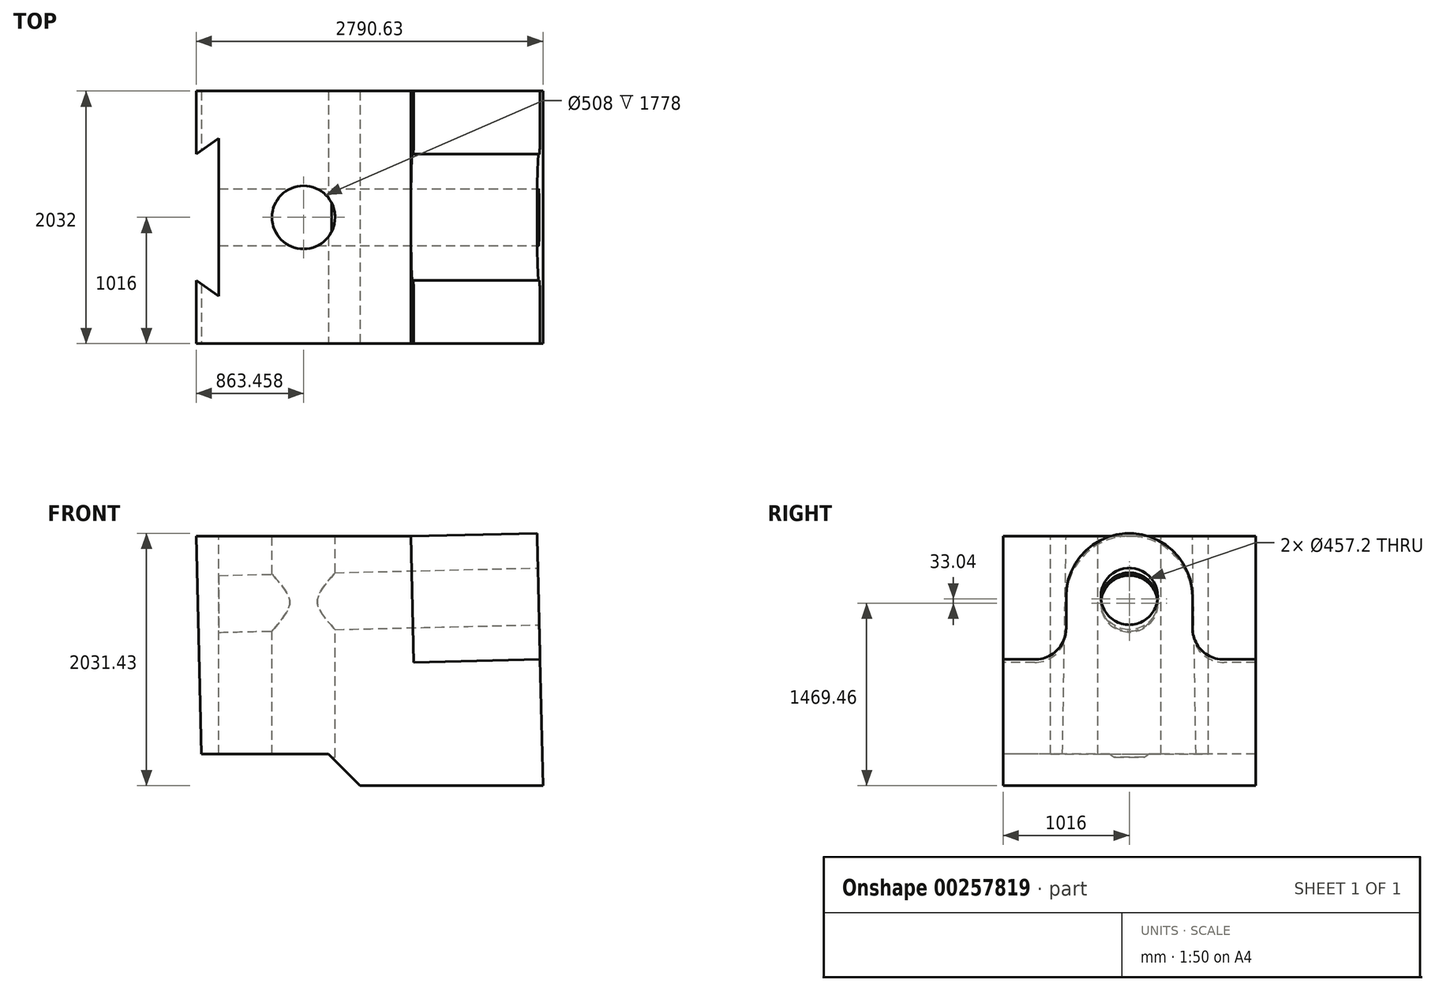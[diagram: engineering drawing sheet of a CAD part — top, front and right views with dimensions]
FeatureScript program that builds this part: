
annotation { "Feature Type Name" : "Feature", "Feature Type Description" : "" }
export const myFeature = defineFeature(function(context is Context, id is Id, definition is map)
    precondition{}
    {
        {
            var Q0;
            Q0=qCreatedBy(makeId("Front.planeOp"),FACE);
            var sketch = newSketch(context, id + "F0", { "sketchPlane" : qUnion([Q0])});
            skLineSegment(sketch, "E0", {"start": v(-1059.54, -45.61) * mm, "end": v(413.66, -45.61) * mm});
            skLineSegment(sketch, "E1", {"start": v(413.66, -45.61) * mm, "end": v(365.66, 1985.82) * mm});
            skLineSegment(sketch, "E2", {"start": v(365.66, 1985.82) * mm, "end": v(-2377.54, 1985.82) * mm});
            skLineSegment(sketch, "E3", {"start": v(-2377.54, 1985.82) * mm, "end": v(-2335.54, 208.32) * mm});
            skLineSegment(sketch, "E4", {"start": v(-1059.54, -45.61) * mm, "end": v(-1313.47, 208.32) * mm});
            skLineSegment(sketch, "E5", {"start": v(-2335.54, 208.32) * mm, "end": v(-1313.47, 208.32) * mm});
            skSolve(sketch);
        }
        {
            var Q0;
            Q0 = qSketchRegion(id + "F0", true);
            extrude(context, id + "F1", {"entities" : qUnion([Q0]), "oppositeDirection" : true, "depth" : 2032 * mm});
        }
        {
            var Q0;
            Q0=makeQuery(id+"F1.opExtrude","SWEPT_FACE",FACE,{"disambiguationData":[OSD([sQuery(id+"F0.wireOp",EDGE,"E1")])]});
            var sketch = newSketch(context, id + "F2", { "sketchPlane" : qUnion([Q0])});
            skLineSegment(sketch, "E6", {"start": v(1016, -55.37) * mm, "end": v(1016, 2378.05) * mm, "construction": true});
            skPoint(sketch, "E6.endSnap0", {"position": v(1016, 1976.63) * mm});
            skArc(sketch, "E7", {"start": v(1524, 1468.63) * mm, "mid": v(1016, 1976.63) * mm, "end": v(508, 1468.63) * mm});
            skLineSegment(sketch, "E8", {"start": v(2306.5, 960.63) * mm, "end": v(1524, 960.63) * mm});
            skLineSegment(sketch, "E9", {"start": v(1524, 1468.63) * mm, "end": v(1524, 960.63) * mm});
            skLineSegment(sketch, "E10", {"start": v(508, 1468.63) * mm, "end": v(508, 960.63) * mm});
            skLineSegment(sketch, "E11.trimOffspring", {"start": v(508, 960.63) * mm, "end": v(-735.03, 960.63) * mm});
            skLineSegment(sketch, "E12", {"start": v(0, 1976.63) * mm, "end": v(0, 960.63) * mm});
            skLineSegment(sketch, "E13", {"start": v(0, 1976.63) * mm, "end": v(2032, 1976.63) * mm});
            skLineSegment(sketch, "E14", {"start": v(2032, 1976.63) * mm, "end": v(2032, 960.63) * mm});
            skSolve(sketch);
        }
        {
            var Q0;
            Q0 = qSketchRegion(id + "F2", true);
            var Q1;
            Q1=makeQuery(id+"F1.opExtrude","SWEPT_FACE",FACE,{"disambiguationData":[OSD([sQuery(id+"F0.wireOp",EDGE,"E2")])]});
            extrude(context, id + "F3", {"entities" : qUnion([Q0, Q1]), "operationType" : NewBodyOperationType.REMOVE, "oppositeDirection" : true, "depth" : 1016 * mm});
        }
        {
            var Q0;
            Q0=makeQuery(id+"F3.boolean.opBoolean","COPY",EDGE,{"derivedFrom":makeQuery(id+"F3.opExtrude","SWEPT_EDGE",EDGE,{"disambiguationData":[OSD([sQuery(id+"F2.wireOp",EDGE,"E10"),sQuery(id+"F2.wireOp",EDGE,"E11.trimOffspring")])]})});
            fillet(context, id + "F4", {"entities" : qUnion([Q0]), "radius" : 254 * mm, "tangentPropagation" : true, "allowEdgeOverflow" : false});
        }
        {
            var Q0;
            Q0=makeQuery(id+"F3.boolean.opBoolean","COPY",EDGE,{"derivedFrom":makeQuery(id+"F3.opExtrude","SWEPT_EDGE",EDGE,{"disambiguationData":[OSD([sQuery(id+"F2.wireOp",EDGE,"E8"),sQuery(id+"F2.wireOp",EDGE,"E9")])]})});
            fillet(context, id + "F5", {"entities" : qUnion([Q0]), "radius" : 254 * mm, "tangentPropagation" : true, "allowEdgeOverflow" : false});
        }
        {
            var Q0;
            Q0=makeQuery(id+"F1.opExtrude","SWEPT_FACE",FACE,{"disambiguationData":[OSD([sQuery(id+"F0.wireOp",EDGE,"E1")])]});
            var sketch = newSketch(context, id + "F6", { "sketchPlane" : qUnion([Q0])});
            skCircle(sketch, "E15", {"center": v(1016, 1468.63) * mm, "radius": 228.6 * mm});
            skSolve(sketch);
        }
        {
            var Q0;
            Q0 = qSketchRegion(id + "F6", true);
            extrude(context, id + "F7", {"entities" : qUnion([Q0]), "operationType" : NewBodyOperationType.REMOVE, "oppositeDirection" : true, "depth" : 2743.2 * mm});
        }
        {
            var Q0;
            Q0=makeQuery(id+"F3.boolean.opBoolean","COPY",FACE,{"derivedFrom":makeQuery(id+"F3.opExtrude","CAP_FACE",FACE,{"disambiguationData":[OSD([sQuery(id+"F0.wireOp",EDGE,"E2")]),OD(0.0)],"isStart":false})});
            var sketch = newSketch(context, id + "F8", { "sketchPlane" : qUnion([Q0])});
            skLineSegment(sketch, "E16", {"start": v(-1513.51, 2032) * mm, "end": v(-1513.51, 551.9) * mm, "construction": true});
            skLineSegment(sketch, "E17", {"start": v(-2376.97, 1016) * mm, "end": v(-1513.51, 1016) * mm, "construction": true});
            skCircle(sketch, "E18", {"center": v(-1513.51, 1016) * mm, "radius": 254 * mm});
            skSolve(sketch);
        }
        {
            var Q0;
            Q0 = qSketchRegion(id + "F8", true);
            extrude(context, id + "F9", {"entities" : qUnion([Q0]), "operationType" : NewBodyOperationType.REMOVE, "oppositeDirection" : true, "depth" : 1778 * mm});
        }
        {
            var Q0;
            Q0 = qSketchRegion(id + "F8", true);
            extrude(context, id + "F10", {"entities" : qUnion([Q0]), "operationType" : NewBodyOperationType.REMOVE, "oppositeDirection" : true, "depth" : 1778 * mm});
        }
        {
            var Q0;
            Q0=makeQuery(id+"F3.boolean.opBoolean","COPY",FACE,{"derivedFrom":makeQuery(id+"F3.opExtrude","CAP_FACE",FACE,{"disambiguationData":[OSD([sQuery(id+"F0.wireOp",EDGE,"E2")]),OD(0.0)],"isStart":false})});
            var sketch = newSketch(context, id + "F11", { "sketchPlane" : qUnion([Q0])});
            skLineSegment(sketch, "E19", {"start": v(-2376.97, 1016) * mm, "end": v(-650.05, 1016) * mm, "construction": true});
            skLineSegment(sketch, "E20", {"start": v(-2194.8, 1016) * mm, "end": v(-2194.8, 1651) * mm});
            skLineSegment(sketch, "E21.MirrorCS", {"start": v(-2194.8, 1016) * mm, "end": v(-2194.8, 381) * mm});
            skLineSegment(sketch, "E22", {"start": v(-2376.97, 1016) * mm, "end": v(-2376.97, 1524) * mm});
            skLineSegment(sketch, "E23.MirrorCS", {"start": v(-2376.97, 1016) * mm, "end": v(-2376.97, 508) * mm});
            skLineSegment(sketch, "E24", {"start": v(-2376.97, 508) * mm, "end": v(-2194.8, 381) * mm});
            skLineSegment(sketch, "E25", {"start": v(-2376.97, 1524) * mm, "end": v(-2194.8, 1651) * mm});
            skSolve(sketch);
        }
        {
            var Q0;
            Q0 = qSketchRegion(id + "F11", true);
            extrude(context, id + "F12", {"entities" : qUnion([Q0]), "operationType" : NewBodyOperationType.REMOVE, "oppositeDirection" : true, "depth" : 1778 * mm});
        }
    });
